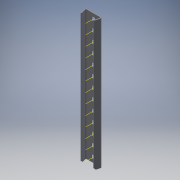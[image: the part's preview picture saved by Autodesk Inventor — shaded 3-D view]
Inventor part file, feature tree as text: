
AUTODESK INVENTOR PART (.ipt)
format: ipt  version: 2017 SP1 (Build 210196100, 196)  size: 423,424 bytes
history: native  units: in
note: dims shown in document units (in); Inventor stores cm internally (conversion verified against a paired STEP export)
features: other x17, boolean_combine x1, extrude x1, pattern_linear x1, imported_body x1, sketch x1
ambient origin geometry x8: Origin, YZ Plane, XZ Plane, XY Plane, X Axis, Y Axis, Z Axis, Center Point
bodies: Body1 (feature_tree)
feature tree (22):
  boolean_combine  "Combine1"
  other  "Linear Slide"
  other  "Work Axis1"
  extrude  "Extrusion1"  TaperAngle=0.0deg  [1 undecoded]
  pattern_linear  "Rectangular Pattern1"  Spacing1=0.0in  [1 undecoded]
  other  "bottom plane"
  other  "top plane"
  imported_body  "Base1"
  other  "Work Point1"
  other  "Work Axis2"
  sketch  "Sketch1"  dims[d0=5.1181in d2=0.5in d4=0.0in d5=0.0in d6=0.0in d8=0.0in]
  other  "Work Axis46"
  other  "Work Axis47"
  other  "Work Axis48"
  other  "Work Axis49"
  other  "Work Axis50"
  other  "Work Axis51"
  other  "Work Axis52"
  other  "Work Axis102"
  other  "Work Axis103"
  other  "Work Axis104"
  other  "Work Axis105"
note: 2 required parameter values undecoded (feature->parameter linkage not recoverable at this tier; creation-order binding heuristic only, values carry confidence <= 0.55)
